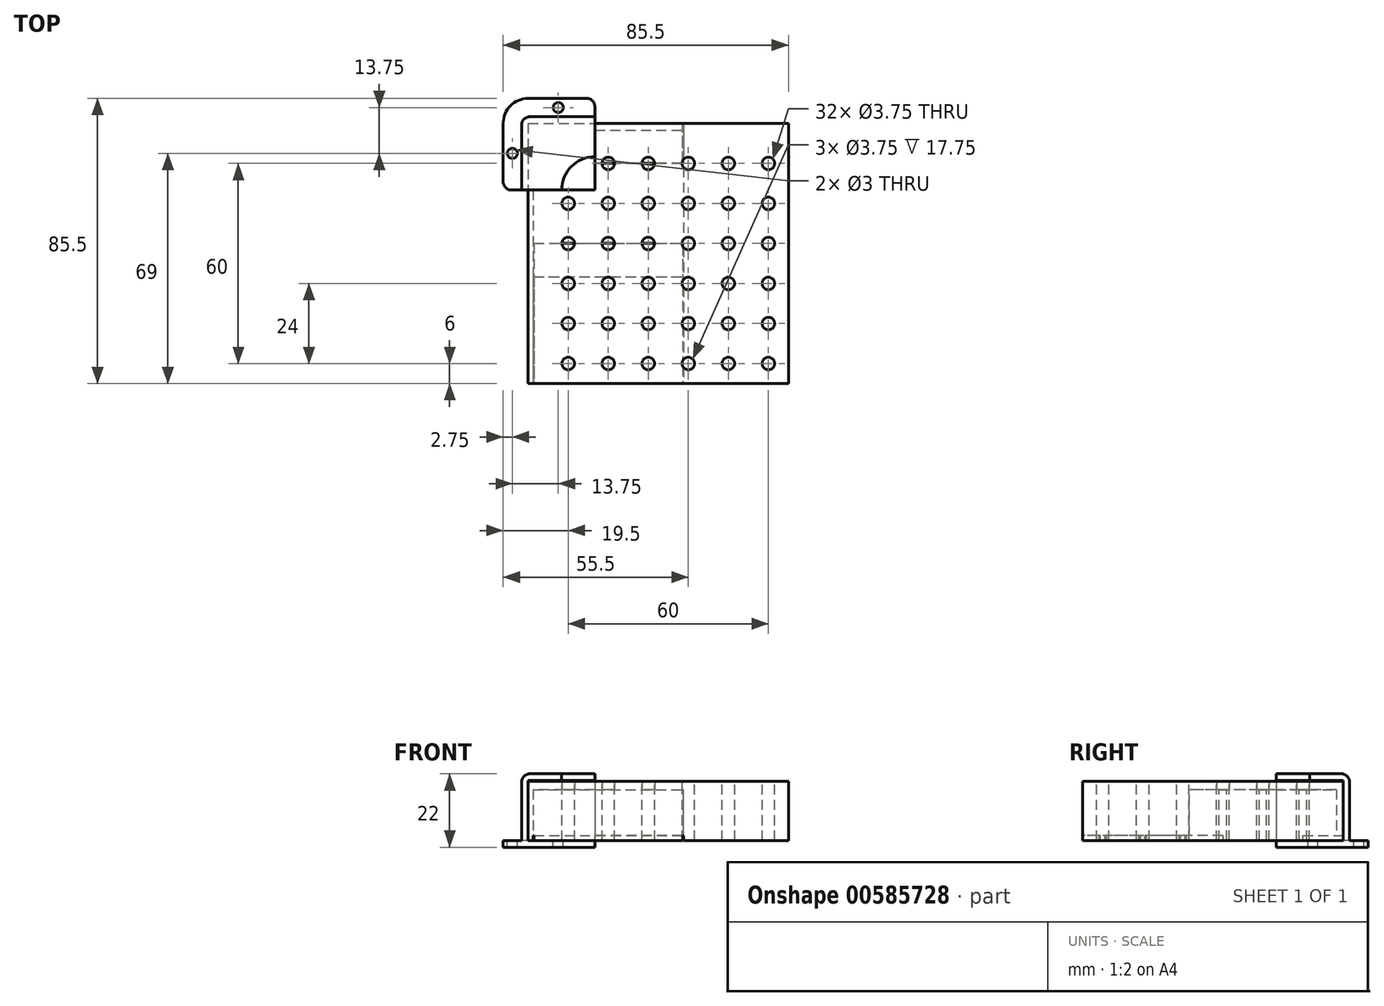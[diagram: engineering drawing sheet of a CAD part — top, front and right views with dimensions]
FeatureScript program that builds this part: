
annotation { "Feature Type Name" : "Feature", "Feature Type Description" : "" }
export const myFeature = defineFeature(function(context is Context, id is Id, definition is map)
    precondition{}
    {
        {
            var Q0;
            Q0=qCreatedBy(makeId("Top.planeOp"),FACE);
            var sketch = newSketch(context, id + "F0", { "sketchPlane" : qUnion([Q0])});
            skCircle(sketch, "E0", {"center": v(-12, 12) * mm, "radius": 1.88 * mm});
            skCircle(sketch, "E1", {"center": v(0, 12) * mm, "radius": 1.88 * mm});
            skCircle(sketch, "E2", {"center": v(12, 12) * mm, "radius": 1.88 * mm});
            skCircle(sketch, "E3", {"center": v(-12, 0) * mm, "radius": 1.88 * mm});
            skCircle(sketch, "E4", {"center": v(0, 0) * mm, "radius": 1.88 * mm});
            skCircle(sketch, "E5", {"center": v(12, 0) * mm, "radius": 1.88 * mm});
            skCircle(sketch, "E6", {"center": v(-12, -12) * mm, "radius": 1.88 * mm});
            skCircle(sketch, "E7", {"center": v(0, -12) * mm, "radius": 1.88 * mm});
            skCircle(sketch, "E8", {"center": v(12, -12) * mm, "radius": 1.88 * mm});
            skLineSegment(sketch, "E9.bottom", {"start": v(-24, -24) * mm, "end": v(24, -24) * mm});
            skLineSegment(sketch, "E9.top", {"start": v(-24, 24) * mm, "end": v(24, 24) * mm});
            skLineSegment(sketch, "E9.left", {"start": v(-24, -24) * mm, "end": v(-24, 24) * mm});
            skLineSegment(sketch, "E9.right", {"start": v(24, -24) * mm, "end": v(24, 24) * mm});
            skSolve(sketch);
        }
        {
            var Q0;
            Q0=makeQuery(id+"F0.imprint","IMPRINT",FACE,{"disambiguationData":[TD([[makeQuery(id+"F0.imprint","IMPRINT",EDGE,{"derivedFrom":sQuery(id+"F0.wireOp",EDGE,"E0")}),-1.0]])]});
            extrude(context, id + "F1", {"entities" : qUnion([Q0]), "depth" : 17.75 * mm, "offsetDistance" : 25 * mm});
        }
        {
            var Q0;
            Q0=makeQuery(id+"F1.opExtrude","CAP_FACE",FACE,{"disambiguationData":[OSD([sQuery(id+"F0.wireOp",EDGE,"E0"),sQuery(id+"F0.wireOp",EDGE,"E1"),sQuery(id+"F0.wireOp",EDGE,"E2"),sQuery(id+"F0.wireOp",EDGE,"E3"),sQuery(id+"F0.wireOp",EDGE,"E4"),sQuery(id+"F0.wireOp",EDGE,"E5"),sQuery(id+"F0.wireOp",EDGE,"E6"),sQuery(id+"F0.wireOp",EDGE,"E7"),sQuery(id+"F0.wireOp",EDGE,"E8"),sQuery(id+"F0.wireOp",EDGE,"E9.bottom"),sQuery(id+"F0.wireOp",EDGE,"E9.top"),sQuery(id+"F0.wireOp",EDGE,"E9.left"),sQuery(id+"F0.wireOp",EDGE,"E9.right")])],"isStart":true});
            var sketch = newSketch(context, id + "F2", { "sketchPlane" : qUnion([Q0])});
            skLineSegment(sketch, "E10.bottom", {"start": v(-22.5, -12) * mm, "end": v(22.5, -12) * mm});
            skLineSegment(sketch, "E10.top", {"start": v(-22.5, 12) * mm, "end": v(22.5, 12) * mm});
            skLineSegment(sketch, "E10.left", {"start": v(-22.5, -12) * mm, "end": v(-22.5, 12) * mm});
            skLineSegment(sketch, "E10.right", {"start": v(22.5, -12) * mm, "end": v(22.5, 12) * mm});
            skPoint(sketch, "E10.middle", {"position": v(0, 0) * mm});
            skSolve(sketch);
        }
        {
            var Q0;
            {var subQ0=sQuery(id+"F2.wireOp",EDGE,"E10.left");Q0=makeQuery(id+"F2.imprint","IMPRINT",FACE,{"disambiguationData":[TD([[makeQuery(id+"F2.imprint","IMPRINT",EDGE,{"derivedFrom":subQ0}),-1.0]])]});}
            extrude(context, id + "F3", {"entities" : qUnion([Q0]), "operationType" : NewBodyOperationType.REMOVE, "oppositeDirection" : true, "depth" : (17.75 - 2.5) * mm, "offsetDistance" : 25 * mm});
        }
        {
            var Q0;
            {var subQ0=sQuery(id+"F2.wireOp",EDGE,"E10.top");Q0=makeQuery(id+"F3.boolean.opBoolean","COPY",FACE,{"derivedFrom":makeQuery(id+"F3.opExtrude","SWEPT_FACE",FACE,{"disambiguationData":[OSD([subQ0]),TDD([makeQuery(id+"F2.imprint","IMPRINT",EDGE,{"disambiguationData":[TD([[makeQuery(id+"F2.imprint","INTERSECT",VERTEX,{"derivedFrom":[subQ0,sQuery(id+"F2.wireOp",EDGE,"E10.left")]}),-1.0]])],"derivedFrom":subQ0})])]})});}
            var sketch = newSketch(context, id + "F4", { "sketchPlane" : qUnion([Q0])});
            skLineSegment(sketch, "E11.bottom", {"start": v(22.5, 1.5) * mm, "end": v(-22.5, 1.5) * mm});
            skLineSegment(sketch, "E11.top", {"start": v(22.5, 15.25) * mm, "end": v(-22.5, 15.25) * mm});
            skLineSegment(sketch, "E11.left", {"start": v(22.5, 1.5) * mm, "end": v(22.5, 15.25) * mm});
            skLineSegment(sketch, "E11.right", {"start": v(-22.5, 1.5) * mm, "end": v(-22.5, 15.25) * mm});
            skSolve(sketch);
        }
        {
            var Q0;
            {var subQ0=sQuery(id+"F4.wireOp",EDGE,"E11.left");Q0=makeQuery(id+"F4.imprint","IMPRINT",FACE,{"disambiguationData":[TD([[makeQuery(id+"F4.imprint","IMPRINT",EDGE,{"derivedFrom":subQ0}),-1.0]])]});}
            var Q1;
            {var subQ0=sQuery(id+"F4.wireOp",EDGE,"E11.right");Q1=makeQuery(id+"F4.imprint","IMPRINT",FACE,{"disambiguationData":[TD([[makeQuery(id+"F4.imprint","IMPRINT",EDGE,{"derivedFrom":subQ0}),-1.0]])]});}
            extrude(context, id + "F5", {"entities" : qUnion([Q0, Q1]), "operationType" : NewBodyOperationType.REMOVE, "oppositeDirection" : true, "depth" : (11.5 - 1.5) * mm, "offsetDistance" : 25 * mm});
        }
        {
            var Q0;
            Q0=makeQuery(id+"F1.opExtrude","CAP_FACE",FACE,{"disambiguationData":[OSD([sQuery(id+"F0.wireOp",EDGE,"E0"),sQuery(id+"F0.wireOp",EDGE,"E1"),sQuery(id+"F0.wireOp",EDGE,"E2"),sQuery(id+"F0.wireOp",EDGE,"E3"),sQuery(id+"F0.wireOp",EDGE,"E4"),sQuery(id+"F0.wireOp",EDGE,"E5"),sQuery(id+"F0.wireOp",EDGE,"E6"),sQuery(id+"F0.wireOp",EDGE,"E7"),sQuery(id+"F0.wireOp",EDGE,"E8"),sQuery(id+"F0.wireOp",EDGE,"E9.bottom"),sQuery(id+"F0.wireOp",EDGE,"E9.top"),sQuery(id+"F0.wireOp",EDGE,"E9.left"),sQuery(id+"F0.wireOp",EDGE,"E9.right")])],"isStart":true});
            var sketch = newSketch(context, id + "F6", { "sketchPlane" : qUnion([Q0])});
            skLineSegment(sketch, "E12.bottom", {"start": v(24, 24) * mm, "end": v(-24, 24) * mm});
            skLineSegment(sketch, "E12.top", {"start": v(24, 12) * mm, "end": v(-24, 12) * mm});
            skLineSegment(sketch, "E12.left", {"start": v(24, 24) * mm, "end": v(24, 12) * mm});
            skLineSegment(sketch, "E12.right", {"start": v(-24, 24) * mm, "end": v(-24, 12) * mm});
            skPoint(sketch, "E13.oppositeSnap0", {"position": v(18.19, -12) * mm});
            skLineSegment(sketch, "E13.bottom", {"start": v(24, -24) * mm, "end": v(-24, -24) * mm});
            skLineSegment(sketch, "E13.top", {"start": v(24, -12) * mm, "end": v(-24, -12) * mm});
            skLineSegment(sketch, "E13.left", {"start": v(24, -24) * mm, "end": v(24, -12) * mm});
            skLineSegment(sketch, "E13.right", {"start": v(-24, -24) * mm, "end": v(-24, -12) * mm});
            skSolve(sketch);
        }
        {
            var Q0;
            Q0 = qSketchRegion(id + "F6", true);
            extrude(context, id + "F7", {"entities" : qUnion([Q0]), "operationType" : NewBodyOperationType.ADD, "oppositeDirection" : true, "depth" : 1.5 * mm, "offsetDistance" : 25 * mm});
        }
        {
            var Q0;
            {var subQ0=sQuery(id+"F2.wireOp",EDGE,"E10.bottom");var subQ2=makeQuery(id+"F1.opExtrude","CAP_EDGE",EDGE,{"disambiguationData":[OSD([sQuery(id+"F0.wireOp",EDGE,"E1")])],"isStart":true});var subQ3=makeQuery(id+"F1.opExtrude","CAP_EDGE",EDGE,{"disambiguationData":[OSD([sQuery(id+"F0.wireOp",EDGE,"E0")])],"isStart":true});Q0=makeQuery(id+"F7.boolean.opBoolean","MERGE",FACE,{"derivedFrom":[makeQuery(id+"F3.boolean.opBoolean","COPY",FACE,{"derivedFrom":makeQuery(id+"F3.opExtrude","SWEPT_FACE",FACE,{"disambiguationData":[OSD([subQ0]),TDD([makeQuery(id+"F2.imprint","IMPRINT",EDGE,{"disambiguationData":[TD([[makeQuery(id+"F2.imprint","INTERSECT",VERTEX,{"derivedFrom":[subQ0,sQuery(id+"F2.wireOp",EDGE,"E10.left")]}),-1.0]])],"derivedFrom":subQ0})])]})}),makeQuery(id+"F3.boolean.opBoolean","COPY",FACE,{"derivedFrom":makeQuery(id+"F3.opExtrude","SWEPT_FACE",FACE,{"disambiguationData":[OSD([subQ0]),TDD([makeQuery(id+"F2.imprint","IMPRINT",EDGE,{"disambiguationData":[TD([[makeQuery(id+"F2.imprint","INTERSECT",VERTEX,{"disambiguationData":[OD(1.0)],"derivedFrom":[subQ3,subQ0]}),-1.0]])],"derivedFrom":subQ0})])]})}),makeQuery(id+"F3.boolean.opBoolean","COPY",FACE,{"derivedFrom":makeQuery(id+"F3.opExtrude","SWEPT_FACE",FACE,{"disambiguationData":[OSD([subQ0]),TDD([makeQuery(id+"F2.imprint","IMPRINT",EDGE,{"disambiguationData":[TD([[makeQuery(id+"F2.imprint","INTERSECT",VERTEX,{"disambiguationData":[OD(1.0)],"derivedFrom":[subQ2,subQ0]}),-1.0]])],"derivedFrom":subQ0})])]})}),makeQuery(id+"F3.boolean.opBoolean","COPY",FACE,{"derivedFrom":makeQuery(id+"F3.opExtrude","SWEPT_FACE",FACE,{"disambiguationData":[OSD([subQ0]),TDD([makeQuery(id+"F2.imprint","IMPRINT",EDGE,{"disambiguationData":[TD([[makeQuery(id+"F2.imprint","INTERSECT",VERTEX,{"derivedFrom":[subQ0,sQuery(id+"F2.wireOp",EDGE,"E10.right")]}),1.0]])],"derivedFrom":subQ0})])]})}),makeQuery(id+"F7.opExtrude","SWEPT_FACE",FACE,{"disambiguationData":[OSD([sQuery(id+"F6.wireOp",EDGE,"E13.top")])]})]});}
            var sketch = newSketch(context, id + "F8", { "sketchPlane" : qUnion([Q0])});
            skLineSegment(sketch, "E14.bottom", {"start": v(-22.5, 15.25) * mm, "end": v(22.5, 15.25) * mm});
            skLineSegment(sketch, "E14.top", {"start": v(-22.5, 1.5) * mm, "end": v(22.5, 1.5) * mm});
            skLineSegment(sketch, "E14.left", {"start": v(-22.5, 15.25) * mm, "end": v(-22.5, 1.5) * mm});
            skLineSegment(sketch, "E14.right", {"start": v(22.5, 15.25) * mm, "end": v(22.5, 1.5) * mm});
            skSolve(sketch);
        }
        {
            var Q0;
            Q0 = qSketchRegion(id + "F8", true);
            extrude(context, id + "F9", {"entities" : qUnion([Q0]), "operationType" : NewBodyOperationType.REMOVE, "oppositeDirection" : true, "depth" : (11.5 - 1.5) * mm, "offsetDistance" : 25 * mm});
        }
        {
            var Q0;
            Q0=makeQuery(id+"F7.boolean.opBoolean","MERGE",FACE,{"derivedFrom":[makeQuery(id+"F1.opExtrude","CAP_FACE",FACE,{"disambiguationData":[OSD([sQuery(id+"F0.wireOp",EDGE,"E0"),sQuery(id+"F0.wireOp",EDGE,"E1"),sQuery(id+"F0.wireOp",EDGE,"E2"),sQuery(id+"F0.wireOp",EDGE,"E3"),sQuery(id+"F0.wireOp",EDGE,"E4"),sQuery(id+"F0.wireOp",EDGE,"E5"),sQuery(id+"F0.wireOp",EDGE,"E6"),sQuery(id+"F0.wireOp",EDGE,"E7"),sQuery(id+"F0.wireOp",EDGE,"E8"),sQuery(id+"F0.wireOp",EDGE,"E9.bottom"),sQuery(id+"F0.wireOp",EDGE,"E9.top"),sQuery(id+"F0.wireOp",EDGE,"E9.left"),sQuery(id+"F0.wireOp",EDGE,"E9.right")])],"isStart":true}),makeQuery(id+"F7.opExtrude","CAP_FACE",FACE,{"disambiguationData":[OSD([sQuery(id+"F6.wireOp",EDGE,"E12.bottom"),sQuery(id+"F6.wireOp",EDGE,"E12.top"),sQuery(id+"F6.wireOp",EDGE,"E12.left"),sQuery(id+"F6.wireOp",EDGE,"E12.right")])],"isStart":true}),makeQuery(id+"F7.opExtrude","CAP_FACE",FACE,{"disambiguationData":[OSD([sQuery(id+"F6.wireOp",EDGE,"E13.bottom"),sQuery(id+"F6.wireOp",EDGE,"E13.top"),sQuery(id+"F6.wireOp",EDGE,"E13.left"),sQuery(id+"F6.wireOp",EDGE,"E13.right")])],"isStart":true})]});
            var sketch = newSketch(context, id + "F10", { "sketchPlane" : qUnion([Q0])});
            skLineSegment(sketch, "E15.bottom", {"start": v(22.5, 12) * mm, "end": v(22.25, 12) * mm});
            skLineSegment(sketch, "E15.top", {"start": v(22.5, 24) * mm, "end": v(22.25, 24) * mm});
            skLineSegment(sketch, "E15.left", {"start": v(22.5, 12) * mm, "end": v(22.5, 24) * mm});
            skLineSegment(sketch, "E15.right", {"start": v(22.25, 12) * mm, "end": v(22.25, 24) * mm});
            skLineSegment(sketch, "E16.bottom", {"start": v(22.5, -12) * mm, "end": v(22.25, -12) * mm});
            skLineSegment(sketch, "E16.top", {"start": v(22.5, -24) * mm, "end": v(22.25, -24) * mm});
            skLineSegment(sketch, "E16.left", {"start": v(22.5, -12) * mm, "end": v(22.5, -24) * mm});
            skLineSegment(sketch, "E16.right", {"start": v(22.25, -12) * mm, "end": v(22.25, -24) * mm});
            skLineSegment(sketch, "E17.bottom", {"start": v(-22.5, -12) * mm, "end": v(-22.25, -12) * mm});
            skLineSegment(sketch, "E17.top", {"start": v(-22.5, -24) * mm, "end": v(-22.25, -24) * mm});
            skLineSegment(sketch, "E17.left", {"start": v(-22.5, -12) * mm, "end": v(-22.5, -24) * mm});
            skLineSegment(sketch, "E17.right", {"start": v(-22.25, -12) * mm, "end": v(-22.25, -24) * mm});
            skLineSegment(sketch, "E18.bottom", {"start": v(-22.5, 12) * mm, "end": v(-22.25, 12) * mm});
            skLineSegment(sketch, "E18.top", {"start": v(-22.5, 24) * mm, "end": v(-22.25, 24) * mm});
            skLineSegment(sketch, "E18.left", {"start": v(-22.5, 12) * mm, "end": v(-22.5, 24) * mm});
            skLineSegment(sketch, "E18.right", {"start": v(-22.25, 12) * mm, "end": v(-22.25, 24) * mm});
            skSolve(sketch);
        }
        {
            var Q0;
            Q0=makeQuery(id+"F10.imprint","IMPRINT",FACE,{"disambiguationData":[TD([[makeQuery(id+"F10.imprint","IMPRINT",EDGE,{"derivedFrom":sQuery(id+"F10.wireOp",EDGE,"E18.bottom")}),1.0]])]});
            var Q1;
            Q1=makeQuery(id+"F10.imprint","IMPRINT",FACE,{"disambiguationData":[TD([[makeQuery(id+"F10.imprint","IMPRINT",EDGE,{"derivedFrom":sQuery(id+"F10.wireOp",EDGE,"E15.bottom")}),1.0]])]});
            var Q2;
            Q2=makeQuery(id+"F10.imprint","IMPRINT",FACE,{"disambiguationData":[TD([[makeQuery(id+"F10.imprint","IMPRINT",EDGE,{"derivedFrom":sQuery(id+"F10.wireOp",EDGE,"E16.bottom")}),-1.0]])]});
            var Q3;
            Q3=makeQuery(id+"F10.imprint","IMPRINT",FACE,{"disambiguationData":[TD([[makeQuery(id+"F10.imprint","IMPRINT",EDGE,{"derivedFrom":sQuery(id+"F10.wireOp",EDGE,"E17.bottom")}),-1.0]])]});
            extrude(context, id + "F11", {"entities" : qUnion([Q0, Q1, Q2, Q3]), "operationType" : NewBodyOperationType.REMOVE, "oppositeDirection" : true, "depth" : 1.5 * mm, "offsetDistance" : 25 * mm});
        }
        {
            var Q0;
            Q0=qCreatedBy(makeId("Top.planeOp"),FACE);
            var sketch = newSketch(context, id + "F12", { "sketchPlane" : qUnion([Q0])});
            skLineSegment(sketch, "E19.bottom", {"start": v(-24, 31.5) * mm, "end": v(-6.5, 31.5) * mm});
            skLineSegment(sketch, "E19.top", {"start": v(-24, 4) * mm, "end": v(-4, 4) * mm});
            skLineSegment(sketch, "E19.left", {"start": v(-31.5, 24) * mm, "end": v(-31.5, 6.5) * mm});
            skLineSegment(sketch, "E19.right", {"start": v(-4, 15.86) * mm, "end": v(-4, 4) * mm});
            skPoint(sketch, "E20.visualSharp", {"position": v(-31.5, 31.5) * mm});
            skArc(sketch, "E20.filletArc", {"start": v(-24, 31.5) * mm, "mid": v(-29.3, 29.3) * mm, "end": v(-31.5, 24) * mm});
            skPoint(sketch, "E21.visualSharp", {"position": v(-4, 31.5) * mm});
            skPoint(sketch, "E22.visualSharp", {"position": v(-31.5, 4) * mm});
            skLineSegment(sketch, "E23.bottom", {"start": v(-4, 4) * mm, "end": v(-26, 4) * mm});
            skLineSegment(sketch, "E23.top", {"start": v(-4, 26) * mm, "end": v(-26, 26) * mm});
            skLineSegment(sketch, "E23.left", {"start": v(-4, 4) * mm, "end": v(-4, 26) * mm});
            skLineSegment(sketch, "E23.right", {"start": v(-26, 4) * mm, "end": v(-26, 26) * mm});
            skLineSegment(sketch, "E24", {"start": v(-26, 4) * mm, "end": v(-29, 4) * mm});
            skLineSegment(sketch, "E25", {"start": v(-31.5, 4) * mm, "end": v(-31.5, 4) * mm});
            skLineSegment(sketch, "E26", {"start": v(-4, 31.5) * mm, "end": v(-4, 31.5) * mm});
            skLineSegment(sketch, "E27", {"start": v(-4, 26) * mm, "end": v(-4, 29) * mm});
            skArc(sketch, "E28.filletArc", {"start": v(-31.5, 6.5) * mm, "mid": v(-30.77, 4.73) * mm, "end": v(-29, 4) * mm});
            skArc(sketch, "E29.filletArc", {"start": v(-4, 29) * mm, "mid": v(-4.73, 30.77) * mm, "end": v(-6.5, 31.5) * mm});
            skCircle(sketch, "E30", {"center": v(-15, 28.75) * mm, "radius": 1.5 * mm});
            skCircle(sketch, "E31", {"center": v(-28.75, 15) * mm, "radius": 1.5 * mm});
            skSolve(sketch);
        }
        {
            var Q0;
            Q0=makeQuery(id+"F12.imprint","IMPRINT",FACE,{"disambiguationData":[TD([[makeQuery(id+"F12.imprint","IMPRINT",EDGE,{"derivedFrom":sQuery(id+"F12.wireOp",EDGE,"E19.bottom")}),-1.0]])]});
            extrude(context, id + "F13", {"entities" : qUnion([Q0]), "oppositeDirection" : true, "depth" : 2 * mm, "offsetDistance" : 25 * mm});
        }
        {
            var Q0;
            {var subQ4=sQuery(id+"F12.wireOp",EDGE,"E23.top");Q0=makeQuery(id+"F12.imprint","IMPRINT",FACE,{"disambiguationData":[TD([[makeQuery(id+"F12.imprint","IMPRINT",EDGE,{"derivedFrom":subQ4}),1.0]])]});}
            extrude(context, id + "F14", {"entities" : qUnion([Q0]), "depth" : 20 * mm, "offsetDistance" : 25 * mm});
        }
        {
            var Q0;
            {var subQ4=sQuery(id+"F12.wireOp",EDGE,"E23.top");Q0=makeQuery(id+"F12.imprint","IMPRINT",FACE,{"disambiguationData":[TD([[makeQuery(id+"F12.imprint","IMPRINT",EDGE,{"derivedFrom":subQ4}),1.0]])]});}
            extrude(context, id + "F15", {"entities" : qUnion([Q0]), "oppositeDirection" : true, "depth" : 2 * mm, "offsetDistance" : 25 * mm});
        }
        {
            var Q0;
            Q0=makeQuery(id+"F14.opExtrude","SWEPT_FACE",FACE,{"disambiguationData":[OSD([sQuery(id+"F12.wireOp",EDGE,"E23.bottom")])]});
            var sketch = newSketch(context, id + "F16", { "sketchPlane" : qUnion([Q0])});
            skLineSegment(sketch, "E32.bottom", {"start": v(-24, 18) * mm, "end": v(-4, 18) * mm});
            skLineSegment(sketch, "E32.top", {"start": v(-24, 0) * mm, "end": v(-4, 0) * mm});
            skLineSegment(sketch, "E32.left", {"start": v(-24, 18) * mm, "end": v(-24, 0) * mm});
            skLineSegment(sketch, "E32.right", {"start": v(-4, 18) * mm, "end": v(-4, 0) * mm});
            skSolve(sketch);
        }
        {
            var Q0;
            Q0 = qSketchRegion(id + "F16", true);
            extrude(context, id + "F17", {"entities" : qUnion([Q0]), "operationType" : NewBodyOperationType.REMOVE, "oppositeDirection" : true, "depth" : 20 * mm, "offsetDistance" : 25 * mm});
        }
        {
            var Q0;
            Q0=makeQuery(id+"F13.opExtrude","SWEPT_BODY",BODY,{"disambiguationData":[OSD([sQuery(id+"F12.wireOp",EDGE,"E19.bottom"),sQuery(id+"F12.wireOp",EDGE,"E19.left"),sQuery(id+"F12.wireOp",EDGE,"E20.filletArc"),sQuery(id+"F12.wireOp",EDGE,"E23.top"),sQuery(id+"F12.wireOp",EDGE,"E23.right"),sQuery(id+"F12.wireOp",EDGE,"E24"),sQuery(id+"F12.wireOp",EDGE,"E27"),sQuery(id+"F12.wireOp",EDGE,"E28.filletArc"),sQuery(id+"F12.wireOp",EDGE,"E29.filletArc")])]});
            var Q1;
            Q1=makeQuery(id+"F14.opExtrude","SWEPT_BODY",BODY,{"disambiguationData":[OSD([sQuery(id+"F12.wireOp",EDGE,"E23.bottom"),sQuery(id+"F12.wireOp",EDGE,"E23.top"),sQuery(id+"F12.wireOp",EDGE,"E23.left"),sQuery(id+"F12.wireOp",EDGE,"E23.right")])]});
            var Q2;
            Q2=makeQuery(id+"F15.opExtrude","SWEPT_BODY",BODY,{"disambiguationData":[OSD([sQuery(id+"F12.wireOp",EDGE,"E23.bottom"),sQuery(id+"F12.wireOp",EDGE,"E23.top"),sQuery(id+"F12.wireOp",EDGE,"E23.left"),sQuery(id+"F12.wireOp",EDGE,"E23.right")])]});
            booleanBodies(context, id + "F18", {"operationType" : BooleanOperationType.UNION, "tools" : qUnion([Q0, Q1, Q2])});
        }
        {
            var Q0;
            Q0=makeQuery(id+"F14.opExtrude","CAP_EDGE",EDGE,{"disambiguationData":[OSD([sQuery(id+"F12.wireOp",EDGE,"E23.right")])],"isStart":false});
            var Q1;
            Q1=makeQuery(id+"F14.opExtrude","CAP_EDGE",EDGE,{"disambiguationData":[OSD([sQuery(id+"F12.wireOp",EDGE,"E23.top")])],"isStart":false});
            var Q2;
            {var subQ0=sQuery(id+"F12.wireOp",EDGE,"E23.right");var subQ1=sQuery(id+"F12.wireOp",EDGE,"E23.top");Q2=makeQuery(id+"F18.opBoolean","MERGE",EDGE,{"derivedFrom":[makeQuery(id+"F14.opExtrude","SWEPT_EDGE",EDGE,{"disambiguationData":[OSD([subQ1,subQ0])]}),makeQuery(id+"F15.opExtrude","SWEPT_EDGE",EDGE,{"disambiguationData":[OSD([subQ1,subQ0])]})]});}
            fillet(context, id + "F19", {"entities" : qUnion([Q0, Q1, Q2]), "radius" : 2.5 * mm, "tangentPropagation" : true, "allowEdgeOverflow" : false});
        }
        {
            var Q0;
            Q0=makeQuery(id+"F14.opExtrude","CAP_FACE",FACE,{"disambiguationData":[OSD([sQuery(id+"F12.wireOp",EDGE,"E23.bottom"),sQuery(id+"F12.wireOp",EDGE,"E23.top"),sQuery(id+"F12.wireOp",EDGE,"E23.left"),sQuery(id+"F12.wireOp",EDGE,"E23.right")])],"isStart":false});
            var sketch = newSketch(context, id + "F20", { "sketchPlane" : qUnion([Q0])});
            skArc(sketch, "E33", {"start": v(-4, 14) * mm, "mid": v(-11.07, 11.07) * mm, "end": v(-14, 4) * mm});
            skSolve(sketch);
        }
        {
            var Q0;
            {var subQ0=sQuery(id+"F20.wireOp",EDGE,"E33");Q0=makeQuery(id+"F20.imprint","IMPRINT",FACE,{"disambiguationData":[TD([[makeQuery(id+"F20.imprint","IMPRINT",EDGE,{"derivedFrom":subQ0}),1.0]])]});}
            extrude(context, id + "F21", {"entities" : qUnion([Q0]), "operationType" : NewBodyOperationType.REMOVE, "endBound" : BoundingType.UP_TO_NEXT, "oppositeDirection" : true, "depth" : 25 * mm, "offsetDistance" : 25 * mm});
        }
        {
            var Q0;
            Q0=makeQuery(id+"F1.opExtrude","SWEPT_FACE",FACE,{"disambiguationData":[OSD([sQuery(id+"F0.wireOp",EDGE,"E9.right")])]});
            extrude(context, id + "F22", {"entities" : qUnion([Q0]), "operationType" : NewBodyOperationType.ADD, "depth" : 25 * mm, "offsetDistance" : 25 * mm});
        }
        {
            var Q0;
            {var subQ0=sQuery(id+"F0.wireOp",EDGE,"E9.bottom");Q0=makeQuery(id+"F22.boolean.opBoolean","MERGE",FACE,{"derivedFrom":[makeQuery(id+"F1.opExtrude","SWEPT_FACE",FACE,{"disambiguationData":[OSD([subQ0])]}),makeQuery(id+"F22.opExtrude","SWEPT_FACE",FACE,{"disambiguationData":[OSD([subQ0,sQuery(id+"F0.wireOp",EDGE,"E9.right")])]})]});}
            extrude(context, id + "F23", {"entities" : qUnion([Q0]), "operationType" : NewBodyOperationType.ADD, "depth" : 25 * mm, "offsetDistance" : 25 * mm});
        }
        {
            var Q0;
            {var subQ0=sQuery(id+"F0.wireOp",EDGE,"E9.right");var subQ1=sQuery(id+"F0.wireOp",EDGE,"E9.bottom");Q0=makeQuery(id+"F23.boolean.opBoolean","MERGE",FACE,{"derivedFrom":[makeQuery(id+"F22.opExtrude","CAP_FACE",FACE,{"disambiguationData":[OSD([subQ0])],"isStart":false}),makeQuery(id+"F23.opExtrude","SWEPT_FACE",FACE,{"disambiguationData":[OSD([subQ1,subQ0]),TDD([makeQuery(id+"F22.opExtrude","CAP_EDGE",EDGE,{"disambiguationData":[OSD([subQ1,subQ0])],"isStart":false})])]})]});}
            extrude(context, id + "F24", {"entities" : qUnion([Q0]), "operationType" : NewBodyOperationType.ADD, "depth" : 5 * mm, "offsetDistance" : 25 * mm});
        }
        {
            var Q0;
            {var subQ0=sQuery(id+"F0.wireOp",EDGE,"E9.right");var subQ1=sQuery(id+"F0.wireOp",EDGE,"E9.bottom");Q0=makeQuery(id+"F24.boolean.opBoolean","MERGE",FACE,{"derivedFrom":[makeQuery(id+"F23.opExtrude","CAP_FACE",FACE,{"disambiguationData":[OSD([subQ1,subQ0])],"isStart":false}),makeQuery(id+"F24.opExtrude","SWEPT_FACE",FACE,{"disambiguationData":[OSD([subQ1,subQ0]),TDD([makeQuery(id+"F23.opExtrude","CAP_EDGE",EDGE,{"disambiguationData":[OSD([subQ1,subQ0]),TDD([makeQuery(id+"F22.opExtrude","CAP_EDGE",EDGE,{"disambiguationData":[OSD([subQ1,subQ0])],"isStart":false})])],"isStart":false})])]})]});}
            extrude(context, id + "F25", {"entities" : qUnion([Q0]), "operationType" : NewBodyOperationType.ADD, "depth" : 5 * mm, "offsetDistance" : 25 * mm});
        }
        {
            var Q0;
            {var subQ0=sQuery(id+"F0.wireOp",EDGE,"E9.right");var subQ1=sQuery(id+"F0.wireOp",EDGE,"E9.bottom");Q0=makeQuery(id+"F23.boolean.opBoolean","MERGE",FACE,{"derivedFrom":[makeQuery(id+"F22.boolean.opBoolean","MERGE",FACE,{"derivedFrom":[makeQuery(id+"F1.opExtrude","CAP_FACE",FACE,{"disambiguationData":[OSD([sQuery(id+"F0.wireOp",EDGE,"E0"),sQuery(id+"F0.wireOp",EDGE,"E1"),sQuery(id+"F0.wireOp",EDGE,"E2"),sQuery(id+"F0.wireOp",EDGE,"E3"),sQuery(id+"F0.wireOp",EDGE,"E4"),sQuery(id+"F0.wireOp",EDGE,"E5"),sQuery(id+"F0.wireOp",EDGE,"E6"),sQuery(id+"F0.wireOp",EDGE,"E7"),sQuery(id+"F0.wireOp",EDGE,"E8"),subQ1,sQuery(id+"F0.wireOp",EDGE,"E9.top"),sQuery(id+"F0.wireOp",EDGE,"E9.left"),subQ0])],"isStart":false}),makeQuery(id+"F22.opExtrude","SWEPT_FACE",FACE,{"disambiguationData":[OSD([subQ0]),TDD([makeQuery(id+"F1.opExtrude","CAP_EDGE",EDGE,{"disambiguationData":[OSD([subQ0])],"isStart":false})])]})]}),makeQuery(id+"F23.opExtrude","SWEPT_FACE",FACE,{"disambiguationData":[OSD([subQ1,subQ0]),TDD([makeQuery(id+"F22.boolean.opBoolean","MERGE",EDGE,{"derivedFrom":[makeQuery(id+"F1.opExtrude","CAP_EDGE",EDGE,{"disambiguationData":[OSD([subQ1])],"isStart":false}),makeQuery(id+"F22.opExtrude","SWEPT_EDGE",EDGE,{"disambiguationData":[OSD([subQ1,subQ0]),TDD([makeQuery(id+"F1.opExtrude","CAP_VERTEX",VERTEX,{"disambiguationData":[OSD([subQ1,subQ0])],"isStart":false})])]})]})])]})]});}
            var sketch = newSketch(context, id + "F26", { "sketchPlane" : qUnion([Q0])});
            skCircle(sketch, "E34", {"center": v(24, 12) * mm, "radius": 1.87 * mm});
            skCircle(sketch, "E35", {"center": v(36, 12) * mm, "radius": 1.87 * mm});
            skCircle(sketch, "E36", {"center": v(48, 12) * mm, "radius": 1.87 * mm});
            skCircle(sketch, "E37", {"center": v(24, 0) * mm, "radius": 1.87 * mm});
            skCircle(sketch, "E38", {"center": v(36, 0) * mm, "radius": 1.87 * mm});
            skCircle(sketch, "E39", {"center": v(48, 0) * mm, "radius": 1.87 * mm});
            skCircle(sketch, "E40", {"center": v(24, -12) * mm, "radius": 1.87 * mm});
            skCircle(sketch, "E41", {"center": v(36, -12) * mm, "radius": 1.87 * mm});
            skCircle(sketch, "E42", {"center": v(48, -12) * mm, "radius": 1.87 * mm});
            skCircle(sketch, "E43", {"center": v(48, -24) * mm, "radius": 1.88 * mm});
            skCircle(sketch, "E44", {"center": v(36, -24) * mm, "radius": 1.88 * mm});
            skCircle(sketch, "E45", {"center": v(24, -24) * mm, "radius": 1.88 * mm});
            skCircle(sketch, "E46", {"center": v(12, -24) * mm, "radius": 1.88 * mm});
            skCircle(sketch, "E47", {"center": v(0, -24) * mm, "radius": 1.88 * mm});
            skCircle(sketch, "E48", {"center": v(-12, -24) * mm, "radius": 1.88 * mm});
            skCircle(sketch, "E49", {"center": v(48, -36) * mm, "radius": 1.88 * mm});
            skCircle(sketch, "E50", {"center": v(36, -36) * mm, "radius": 1.88 * mm});
            skCircle(sketch, "E51", {"center": v(24, -36) * mm, "radius": 1.88 * mm});
            skCircle(sketch, "E52", {"center": v(12, -36) * mm, "radius": 1.88 * mm});
            skCircle(sketch, "E53", {"center": v(0, -36) * mm, "radius": 1.88 * mm});
            skCircle(sketch, "E54", {"center": v(-12, -36) * mm, "radius": 1.88 * mm});
            skCircle(sketch, "E55", {"center": v(48, -48) * mm, "radius": 1.88 * mm});
            skCircle(sketch, "E56", {"center": v(36, -48) * mm, "radius": 1.88 * mm});
            skCircle(sketch, "E57", {"center": v(24, -48) * mm, "radius": 1.88 * mm});
            skCircle(sketch, "E58", {"center": v(12, -48) * mm, "radius": 1.88 * mm});
            skCircle(sketch, "E59", {"center": v(0, -48) * mm, "radius": 1.88 * mm});
            skCircle(sketch, "E60", {"center": v(-12, -48) * mm, "radius": 1.88 * mm});
            skSolve(sketch);
        }
        {
            var Q0;
            Q0 = qSketchRegion(id + "F26", true);
            extrude(context, id + "F27", {"entities" : qUnion([Q0]), "operationType" : NewBodyOperationType.REMOVE, "endBound" : BoundingType.UP_TO_NEXT, "oppositeDirection" : true, "depth" : 25 * mm, "offsetDistance" : 25 * mm});
        }
    });
